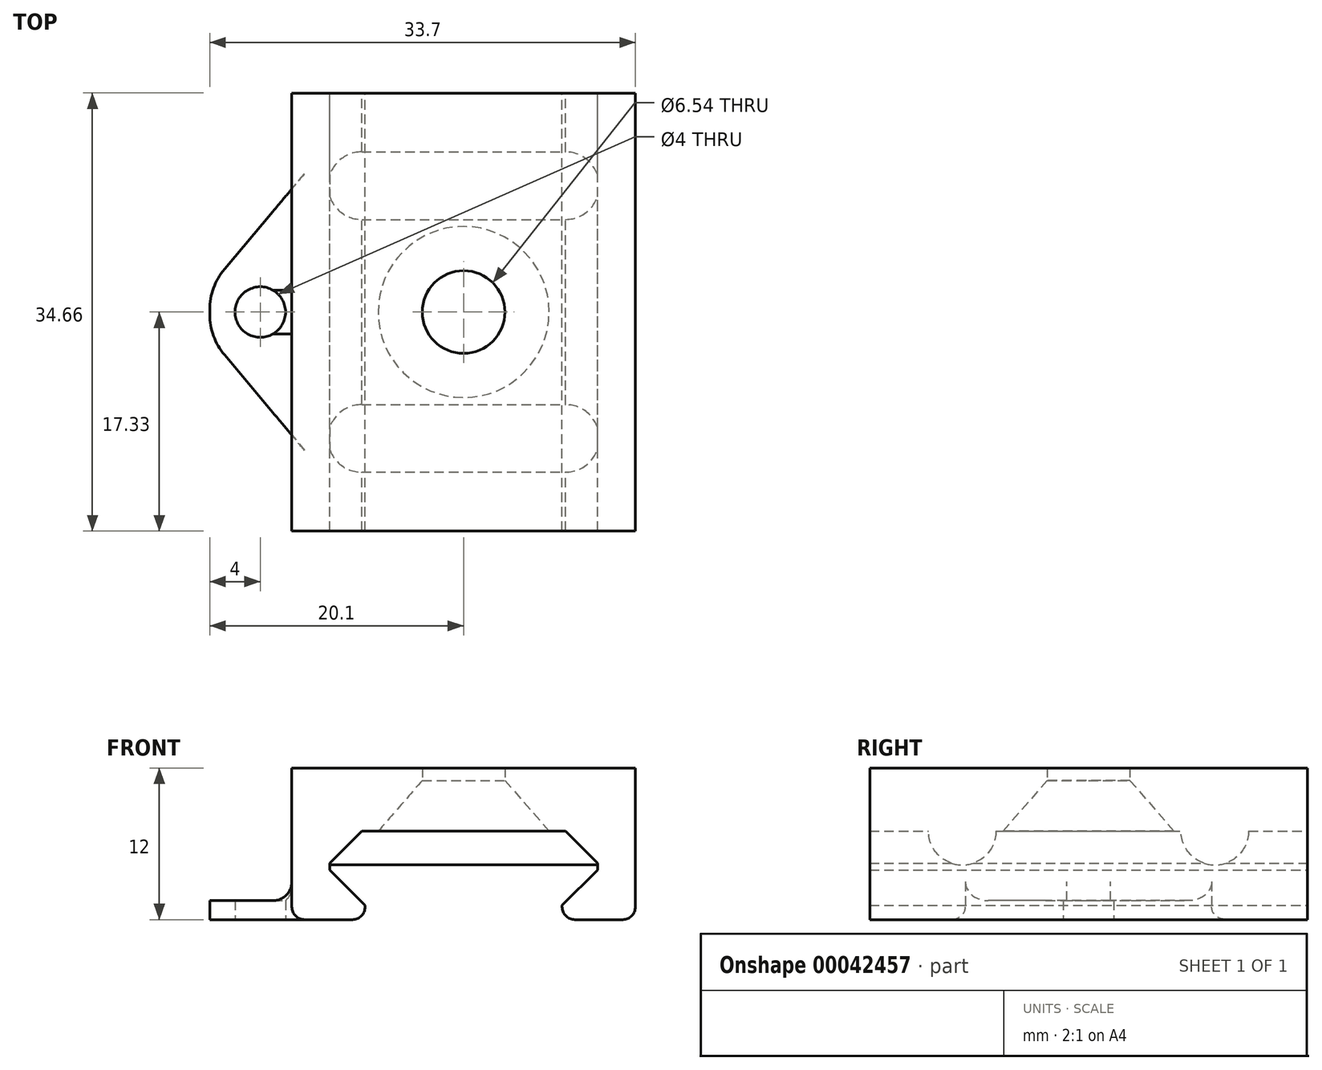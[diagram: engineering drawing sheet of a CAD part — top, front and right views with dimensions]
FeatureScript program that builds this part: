
annotation { "Feature Type Name" : "Feature", "Feature Type Description" : "" }
export const myFeature = defineFeature(function(context is Context, id is Id, definition is map)
    precondition{}
    {
        {
            var Q0;
            Q0=qCreatedBy(makeId("Front.planeOp"),FACE);
            var sketch = newSketch(context, id + "F0", { "sketchPlane" : qUnion([Q0])});
            skLineSegment(sketch, "E0", {"start": v(-10.6, -2.8) * mm, "end": v(10.6, -2.8) * mm, "construction": true});
            skLineSegment(sketch, "E1", {"start": v(-10.6, -3.07) * mm, "end": v(-10.6, -2.53) * mm});
            skLineSegment(sketch, "E2", {"start": v(-10.6, -2.53) * mm, "end": v(-8.07, 0) * mm});
            skLineSegment(sketch, "E3", {"start": v(-8.07, 0) * mm, "end": v(8.07, 0) * mm});
            skLineSegment(sketch, "E4", {"start": v(8.07, 0) * mm, "end": v(10.6, -2.53) * mm});
            skLineSegment(sketch, "E5", {"start": v(10.6, -2.53) * mm, "end": v(10.6, -3.07) * mm});
            skLineSegment(sketch, "E6", {"start": v(10.6, -3.07) * mm, "end": v(7.8, -5.87) * mm});
            skLineSegment(sketch, "E7", {"start": v(7.8, -5.87) * mm, "end": v(7.8, -7) * mm});
            skLineSegment(sketch, "E8", {"start": v(-7.8, -7) * mm, "end": v(-7.8, -5.87) * mm});
            skLineSegment(sketch, "E9", {"start": v(-7.8, -5.87) * mm, "end": v(-10.6, -3.07) * mm});
            skLineSegment(sketch, "E10", {"start": v(0, 0) * mm, "end": v(0, -7) * mm, "construction": true});
            skLineSegment(sketch, "E11", {"start": v(-8.07, 0) * mm, "end": v(-17.76, 0) * mm, "construction": true});
            skLineSegment(sketch, "E12", {"start": v(8.07, 0) * mm, "end": v(18.28, 0) * mm, "construction": true});
            skLineSegment(sketch, "E13", {"start": v(7.8, -7) * mm, "end": v(7.8, 0) * mm, "construction": true});
            skLineSegment(sketch, "E14", {"start": v(-9.5, -4.17) * mm, "end": v(9.5, -4.17) * mm, "construction": true});
            skLineSegment(sketch, "E15", {"start": v(9.5, -1.43) * mm, "end": v(-9.5, -1.43) * mm, "construction": true});
            skLineSegment(sketch, "E16", {"start": v(-9.5, -1.43) * mm, "end": v(-9.5, -4.17) * mm, "construction": true});
            skLineSegment(sketch, "E17", {"start": v(9.5, -1.43) * mm, "end": v(9.5, -4.17) * mm, "construction": true});
            skLineSegment(sketch, "E18", {"start": v(9.5, -4.17) * mm, "end": v(9.5, 0) * mm, "construction": true});
            skPoint(sketch, "E19.visualSharp", {"position": v(-7.8, -7) * mm});
            skPoint(sketch, "E20.visualSharp", {"position": v(7.8, -7) * mm});
            skLineSegment(sketch, "E21", {"start": v(-7.8, -5.87) * mm, "end": v(7.8, -5.87) * mm, "construction": true});
            skLineSegment(sketch, "E22", {"start": v(-7.8, -7) * mm, "end": v(7.8, -7) * mm, "construction": true});
            skPoint(sketch, "E23", {"position": v(0, -7) * mm});
            skLineSegment(sketch, "E24", {"start": v(-7.8, -7) * mm, "end": v(-13.6, -7) * mm});
            skLineSegment(sketch, "E25", {"start": v(-13.6, -7) * mm, "end": v(-13.6, 5) * mm});
            skLineSegment(sketch, "E26", {"start": v(-13.6, 5) * mm, "end": v(13.6, 5) * mm});
            skLineSegment(sketch, "E27", {"start": v(13.6, 5) * mm, "end": v(13.6, -7) * mm});
            skLineSegment(sketch, "E28", {"start": v(13.6, -7) * mm, "end": v(7.8, -7) * mm});
            skLineSegment(sketch, "E29", {"start": v(10.6, -2.8) * mm, "end": v(13.6, -2.8) * mm, "construction": true});
            skLineSegment(sketch, "E30", {"start": v(-10.6, -2.8) * mm, "end": v(-13.6, -2.8) * mm, "construction": true});
            skLineSegment(sketch, "E31", {"start": v(-8.07, 0) * mm, "end": v(-8.07, 5) * mm, "construction": true});
            skSolve(sketch);
        }
        {
            var Q0;
            Q0=qSketchRegion(id+"F0",true);
            extrude(context, id + "F1", {"entities" : qUnion([Q0]), "depth" : (40 - 5.35) * mm});
        }
        {
            var Q0;
            Q0=makeQuery(id+"F1.opExtrude","SWEPT_BODY",BODY,{"disambiguationData":[OSD([sQuery(id+"F0.wireOp",EDGE,"E1"),sQuery(id+"F0.wireOp",EDGE,"E2"),sQuery(id+"F0.wireOp",EDGE,"E3"),sQuery(id+"F0.wireOp",EDGE,"E4"),sQuery(id+"F0.wireOp",EDGE,"E5"),sQuery(id+"F0.wireOp",EDGE,"E6"),sQuery(id+"F0.wireOp",EDGE,"E7"),sQuery(id+"F0.wireOp",EDGE,"E8"),sQuery(id+"F0.wireOp",EDGE,"E9"),sQuery(id+"F0.wireOp",EDGE,"E24"),sQuery(id+"F0.wireOp",EDGE,"E25"),sQuery(id+"F0.wireOp",EDGE,"E26"),sQuery(id+"F0.wireOp",EDGE,"E27"),sQuery(id+"F0.wireOp",EDGE,"E28")])]});
            transform(context, id + "F2", {"entities" : qUnion([Q0]), "transformType" : TransformType.TRANSLATION_3D, "dx" : 0 * mm, "dy" : ((40 - 5.35) / 2) * mm, "dz" : 0 * mm, "makeCopy" : false});
        }
        {
            var Q0;
            Q0=makeQuery(id+"F1.opExtrude","SWEPT_EDGE",EDGE,{"disambiguationData":[OSD([sQuery(id+"F0.wireOp",EDGE,"E8"),sQuery(id+"F0.wireOp",EDGE,"E24")])]});
            var Q1;
            Q1=makeQuery(id+"F1.opExtrude","SWEPT_EDGE",EDGE,{"disambiguationData":[OSD([sQuery(id+"F0.wireOp",EDGE,"E7"),sQuery(id+"F0.wireOp",EDGE,"E28")])]});
            fillet(context, id + "F3", {"entities" : qUnion([Q0, Q1]), "radius" : 1 * mm, "allowEdgeOverflow" : false});
        }
        {
            var Q0;
            Q0=makeQuery(id+"F1.opExtrude","SWEPT_FACE",FACE,{"disambiguationData":[OSD([sQuery(id+"F0.wireOp",EDGE,"E3")])]});
            var sketch = newSketch(context, id + "F4", { "sketchPlane" : qUnion([Q0])});
            skPoint(sketch, "E32", {"position": v(0, 0) * mm});
            skSolve(sketch);
        }
        {
            var Q0;
            Q0=qCreatedBy(makeId("Right.planeOp"),FACE);
            var sketch = newSketch(context, id + "F5", { "sketchPlane" : qUnion([Q0])});
            skLineSegment(sketch, "E33", {"start": v(0, -2.88) * mm, "end": v(0, 8.77) * mm});
            skLineSegment(sketch, "E34", {"start": v(0, 8.77) * mm, "end": v(3.17, 8.77) * mm});
            skLineSegment(sketch, "E35", {"start": v(3.17, 8.77) * mm, "end": v(3.18, 4.13) * mm, "construction": true});
            skLineSegment(sketch, "E36", {"start": v(3.18, 4.13) * mm, "end": v(6.77, 4.13) * mm, "construction": true});
            skLineSegment(sketch, "E37", {"start": v(6.77, -2.88) * mm, "end": v(0, -2.88) * mm});
            skLineSegment(sketch, "E38", {"start": v(3.18, 4.13) * mm, "end": v(6.77, 0) * mm});
            skLineSegment(sketch, "E39", {"start": v(6.77, 0) * mm, "end": v(0, 0) * mm});
            skLineSegment(sketch, "E40", {"start": v(6.77, -2.88) * mm, "end": v(6.77, 0) * mm});
            skLineSegment(sketch, "E41", {"start": v(6.77, 4.13) * mm, "end": v(6.77, 0) * mm, "construction": true});
            skLineSegment(sketch, "E42", {"start": v(3.27, 8.77) * mm, "end": v(3.27, 4.02) * mm});
            skLineSegment(sketch, "E43", {"start": v(0, 8.77) * mm, "end": v(3.27, 8.77) * mm});
            skSolve(sketch);
        }
        {
            var Q0;
            Q0 = qSketchRegion(id + "F5", true);
            var Q1;
            Q1=sQuery(id+"F5.wireOp",EDGE,"E33");
            revolve(context, id + "F6", {"entities" : qUnion([Q0]), "axis" : qUnion([Q1]), "revolveType" : RevolveType.FULL});
        }
        {
            var Q0;
            Q0=makeQuery(id+"F6.opRevolve","SWEPT_BODY",BODY,{"disambiguationData":[OSD([sQuery(id+"F5.wireOp",EDGE,"E33"),sQuery(id+"F5.wireOp",EDGE,"E37"),sQuery(id+"F5.wireOp",EDGE,"E38"),sQuery(id+"F5.wireOp",EDGE,"E40"),sQuery(id+"F5.wireOp",EDGE,"E42"),sQuery(id+"F5.wireOp",EDGE,"E43")])]});
            var Q1;
            Q1=makeQuery(id+"F1.opExtrude","SWEPT_BODY",BODY,{"disambiguationData":[OSD([sQuery(id+"F0.wireOp",EDGE,"E1"),sQuery(id+"F0.wireOp",EDGE,"E2"),sQuery(id+"F0.wireOp",EDGE,"E3"),sQuery(id+"F0.wireOp",EDGE,"E4"),sQuery(id+"F0.wireOp",EDGE,"E5"),sQuery(id+"F0.wireOp",EDGE,"E6"),sQuery(id+"F0.wireOp",EDGE,"E7"),sQuery(id+"F0.wireOp",EDGE,"E8"),sQuery(id+"F0.wireOp",EDGE,"E9"),sQuery(id+"F0.wireOp",EDGE,"E24"),sQuery(id+"F0.wireOp",EDGE,"E25"),sQuery(id+"F0.wireOp",EDGE,"E26"),sQuery(id+"F0.wireOp",EDGE,"E27"),sQuery(id+"F0.wireOp",EDGE,"E28")])]});
            booleanBodies(context, id + "F7", {"operationType" : BooleanOperationType.SUBTRACTION, "tools" : qUnion([Q0]), "targets" : qUnion([Q1])});
        }
        {
            var Q0;
            Q0=makeQuery(id+"F1.opExtrude","SWEPT_EDGE",EDGE,{"disambiguationData":[OSD([sQuery(id+"F0.wireOp",EDGE,"E24"),sQuery(id+"F0.wireOp",EDGE,"E25")])]});
            var Q1;
            Q1=makeQuery(id+"F1.opExtrude","SWEPT_EDGE",EDGE,{"disambiguationData":[OSD([sQuery(id+"F0.wireOp",EDGE,"E27"),sQuery(id+"F0.wireOp",EDGE,"E28")])]});
            fillet(context, id + "F8", {"entities" : qUnion([Q0, Q1]), "radius" : 1 * mm, "allowEdgeOverflow" : false});
        }
        {
            var Q0;
            Q0=makeQuery(id+"F1.opExtrude","SWEPT_FACE",FACE,{"disambiguationData":[OSD([sQuery(id+"F0.wireOp",EDGE,"E27")])]});
            var sketch = newSketch(context, id + "F9", { "sketchPlane" : qUnion([Q0])});
            skLineSegment(sketch, "E44.0", {"start": v(-17.32, 0) * mm, "end": v(17.32, 0) * mm, "construction": true});
            skLineSegment(sketch, "E45", {"start": v(-17.32, 0) * mm, "end": v(-12.67, 0) * mm, "construction": true});
            skLineSegment(sketch, "E46", {"start": v(-12.67, 0) * mm, "end": v(-7.32, 0) * mm});
            skLineSegment(sketch, "E47.MirrorCS", {"start": v(12.67, 0) * mm, "end": v(7.32, 0) * mm});
            skLineSegment(sketch, "E48.MirrorCS", {"start": v(17.32, 0) * mm, "end": v(12.67, 0) * mm, "construction": true});
            skLineSegment(sketch, "E49", {"start": v(-7.32, 0) * mm, "end": v(-2.67, 0) * mm, "construction": true});
            skLineSegment(sketch, "E50", {"start": v(-2.67, 0) * mm, "end": v(2.68, 0) * mm});
            skLineSegment(sketch, "E51", {"start": v(2.68, 0) * mm, "end": v(7.32, 0) * mm, "construction": true});
            skArc(sketch, "E52", {"start": v(-12.67, 0) * mm, "mid": v(-11.9, -1.9) * mm, "end": v(-10, -2.67) * mm});
            skArc(sketch, "E53", {"start": v(-7.32, 0) * mm, "mid": v(-8.1, -1.9) * mm, "end": v(-10, -2.67) * mm});
            skLineSegment(sketch, "E54", {"start": v(-10, 0) * mm, "end": v(-10, -2.67) * mm, "construction": true});
            skArc(sketch, "E55.MirrorCS", {"start": v(12.67, 0) * mm, "mid": v(11.9, -1.9) * mm, "end": v(10, -2.67) * mm});
            skLineSegment(sketch, "E56.MirrorCS", {"start": v(10, 0) * mm, "end": v(10, -2.67) * mm, "construction": true});
            skArc(sketch, "E57.MirrorCS", {"start": v(7.32, 0) * mm, "mid": v(8.1, -1.9) * mm, "end": v(10, -2.67) * mm});
            skSolve(sketch);
        }
        {
            var Q0;
            Q0 = qSketchRegion(id + "F9", true);
            var Q1;
            Q1=makeQuery(id+"F1.opExtrude","SWEPT_FACE",FACE,{"disambiguationData":[OSD([sQuery(id+"F0.wireOp",EDGE,"E25")])]});
            extrude(context, id + "F10", {"entities" : qUnion([Q0]), "operationType" : NewBodyOperationType.ADD, "endBound" : BoundingType.UP_TO_SURFACE, "oppositeDirection" : true, "endBoundEntityFace" : qUnion([Q1]), "depth" : 25 * mm});
        }
        {
            var Q0;
            Q0=makeQuery(id+"F1.opExtrude","SWEPT_FACE",FACE,{"disambiguationData":[OSD([sQuery(id+"F0.wireOp",EDGE,"E24")])]});
            var sketch = newSketch(context, id + "F11", { "sketchPlane" : qUnion([Q0])});
            skLineSegment(sketch, "E58.0", {"start": v(-12.6, 17.32) * mm, "end": v(-12.6, -17.32) * mm});
            skLineSegment(sketch, "E59", {"start": v(-12.6, 0) * mm, "end": v(-20.1, 0) * mm, "construction": true});
            skPoint(sketch, "E59.endSnap0", {"position": v(-12.6, 0) * mm});
            skLineSegment(sketch, "E60", {"start": v(-20.1, 0.18) * mm, "end": v(-20.1, -0.18) * mm});
            skLineSegment(sketch, "E61", {"start": v(-18.93, -3.4) * mm, "end": v(-12.6, -10.94) * mm});
            skLineSegment(sketch, "E62", {"start": v(-18.93, 3.4) * mm, "end": v(-12.6, 10.94) * mm});
            skLineSegment(sketch, "E63", {"start": v(-20.1, 0) * mm, "end": v(-16.1, 0) * mm, "construction": true});
            skCircle(sketch, "E64", {"center": v(-16.1, 0) * mm, "radius": 2 * mm});
            skPoint(sketch, "E65.visualSharp", {"position": v(-20.1, -2) * mm});
            skArc(sketch, "E65.filletArc", {"start": v(-20.1, -0.18) * mm, "mid": v(-19.8, -1.9) * mm, "end": v(-18.93, -3.4) * mm});
            skPoint(sketch, "E66.visualSharp", {"position": v(-20.1, 2) * mm});
            skArc(sketch, "E66.filletArc", {"start": v(-18.93, 3.4) * mm, "mid": v(-19.8, 1.9) * mm, "end": v(-20.1, 0.18) * mm});
            skSolve(sketch);
        }
        {
            var Q0;
            Q0 = qSketchRegion(id + "F11", true);
            extrude(context, id + "F12", {"entities" : qUnion([Q0]), "oppositeDirection" : true, "depth" : 1.5 * mm});
        }
        {
            var Q0;
            Q0=makeQuery(id+"F1.opExtrude","SWEPT_BODY",BODY,{"disambiguationData":[OSD([sQuery(id+"F0.wireOp",EDGE,"E1"),sQuery(id+"F0.wireOp",EDGE,"E2"),sQuery(id+"F0.wireOp",EDGE,"E3"),sQuery(id+"F0.wireOp",EDGE,"E4"),sQuery(id+"F0.wireOp",EDGE,"E5"),sQuery(id+"F0.wireOp",EDGE,"E6"),sQuery(id+"F0.wireOp",EDGE,"E7"),sQuery(id+"F0.wireOp",EDGE,"E8"),sQuery(id+"F0.wireOp",EDGE,"E9"),sQuery(id+"F0.wireOp",EDGE,"E24"),sQuery(id+"F0.wireOp",EDGE,"E25"),sQuery(id+"F0.wireOp",EDGE,"E26"),sQuery(id+"F0.wireOp",EDGE,"E27"),sQuery(id+"F0.wireOp",EDGE,"E28")])]});
            var Q1;
            Q1=makeQuery(id+"F12.opExtrude","SWEPT_BODY",BODY,{"disambiguationData":[OSD([sQuery(id+"F11.wireOp",EDGE,"E58.0"),sQuery(id+"F11.wireOp",EDGE,"E60"),sQuery(id+"F11.wireOp",EDGE,"E61"),sQuery(id+"F11.wireOp",EDGE,"E62")])]});
            booleanBodies(context, id + "F13", {"operationType" : BooleanOperationType.UNION, "tools" : qUnion([Q0, Q1])});
        }
        {
            var Q0;
            Q0=makeQuery(id+"F13.opBoolean","INTERSECT",EDGE,{"derivedFrom":[makeQuery(id+"F1.opExtrude","SWEPT_FACE",FACE,{"disambiguationData":[OSD([sQuery(id+"F0.wireOp",EDGE,"E25")])]}),makeQuery(id+"F12.opExtrude","CAP_FACE",FACE,{"disambiguationData":[OSD([sQuery(id+"F11.wireOp",EDGE,"E58.0"),sQuery(id+"F11.wireOp",EDGE,"E60"),sQuery(id+"F11.wireOp",EDGE,"E61"),sQuery(id+"F11.wireOp",EDGE,"E62")])],"isStart":false})]});
            fillet(context, id + "F14", {"entities" : qUnion([Q0]), "radius" : 1.5 * mm, "allowEdgeOverflow" : false});
        }
    });
